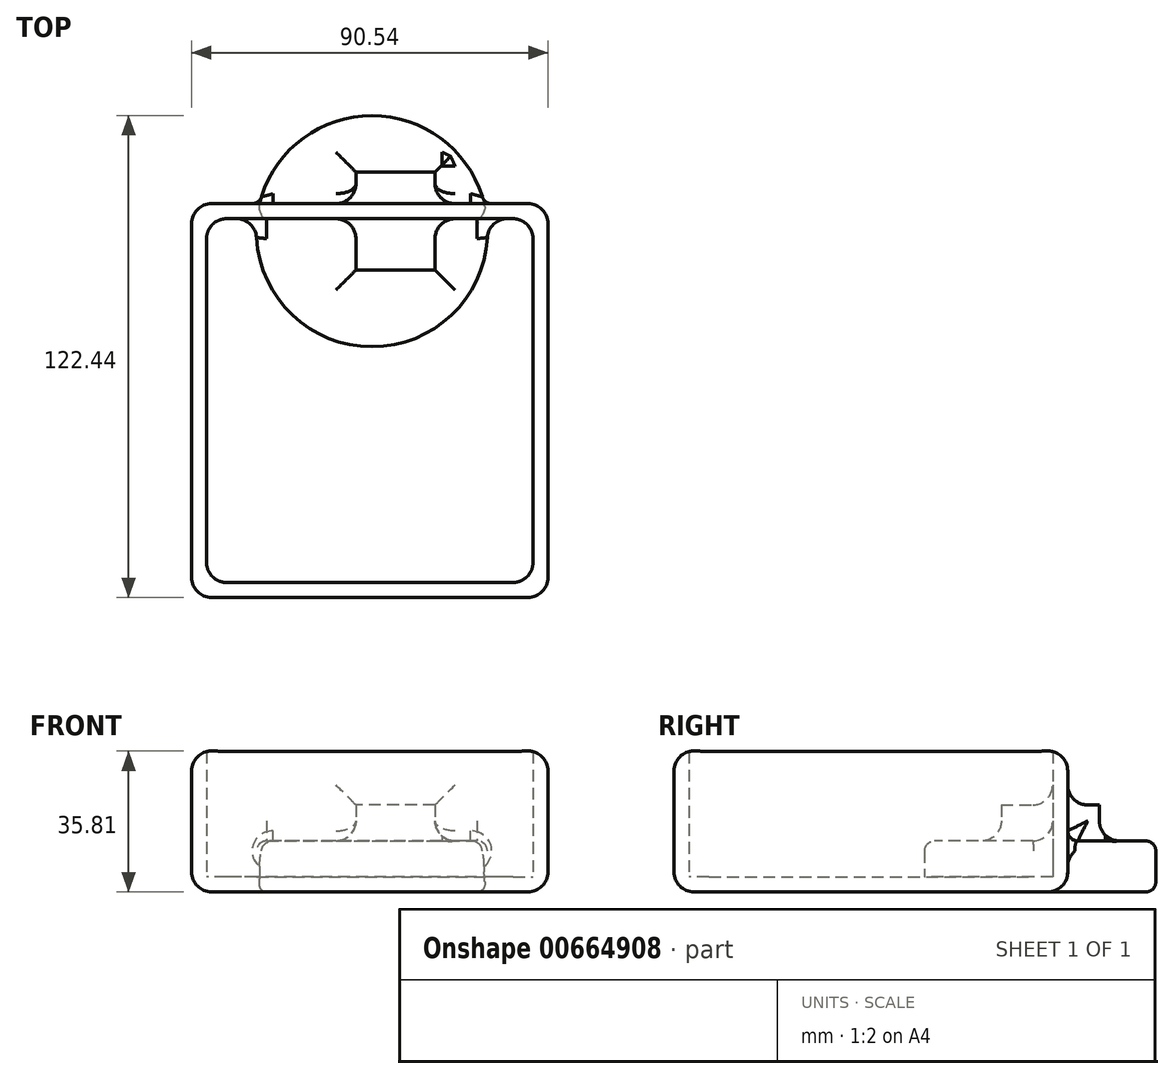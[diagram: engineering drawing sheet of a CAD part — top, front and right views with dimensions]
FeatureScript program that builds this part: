
annotation { "Feature Type Name" : "Feature", "Feature Type Description" : "" }
export const myFeature = defineFeature(function(context is Context, id is Id, definition is map)
    precondition{}
    {
        {
            var Q0;
            Q0=qCreatedBy(makeId("Top.planeOp"),FACE);
            var sketch = newSketch(context, id + "F0", { "sketchPlane" : qUnion([Q0])});
            skLineSegment(sketch, "E0.bottom", {"start": v(36.09, -51.72) * mm, "end": v(-54.45, -51.72) * mm});
            skLineSegment(sketch, "E0.top", {"start": v(36.09, 48.33) * mm, "end": v(-54.45, 48.33) * mm});
            skLineSegment(sketch, "E0.left", {"start": v(36.09, -51.72) * mm, "end": v(36.09, 48.33) * mm});
            skLineSegment(sketch, "E0.right", {"start": v(-54.45, -51.72) * mm, "end": v(-54.45, 48.33) * mm});
            skSolve(sketch);
        }
        {
            var Q0;
            Q0 = qSketchRegion(id + "F0", true);
            extrude(context, id + "F1", {"entities" : qUnion([Q0]), "depth" : 35.81 * mm, "offsetDistance" : 25.4 * mm});
        }
        {
            var Q0;
            Q0=makeQuery(id+"F1.opExtrude","CAP_FACE",FACE,{"disambiguationData":[OSD([sQuery(id+"F0.wireOp",EDGE,"E0.bottom"),sQuery(id+"F0.wireOp",EDGE,"E0.top"),sQuery(id+"F0.wireOp",EDGE,"E0.left"),sQuery(id+"F0.wireOp",EDGE,"E0.right")])],"isStart":false});
            shell(context, id + "F2", {"entities" : qUnion([Q0]), "thickness" : 3.8 * mm});
        }
        {
            var Q0;
            Q0=makeQuery(id+"F1.opExtrude","SWEPT_EDGE",EDGE,{"disambiguationData":[OSD([sQuery(id+"F0.wireOp",EDGE,"E0.bottom"),sQuery(id+"F0.wireOp",EDGE,"E0.left")])]});
            var Q1;
            Q1=makeQuery(id+"F1.opExtrude","SWEPT_EDGE",EDGE,{"disambiguationData":[OSD([sQuery(id+"F0.wireOp",EDGE,"E0.bottom"),sQuery(id+"F0.wireOp",EDGE,"E0.right")])]});
            var Q2;
            Q2=makeQuery(id+"F1.opExtrude","SWEPT_EDGE",EDGE,{"disambiguationData":[OSD([sQuery(id+"F0.wireOp",EDGE,"E0.top"),sQuery(id+"F0.wireOp",EDGE,"E0.left")])]});
            var Q3;
            Q3=makeQuery(id+"F1.opExtrude","SWEPT_EDGE",EDGE,{"disambiguationData":[OSD([sQuery(id+"F0.wireOp",EDGE,"E0.top"),sQuery(id+"F0.wireOp",EDGE,"E0.right")])]});
            var Q4;
            Q4=makeQuery(id+"F2.opShell","OFFSET_EDGE",EDGE,{"disambiguationData":[OSD([sQuery(id+"F0.wireOp",EDGE,"E0.top"),sQuery(id+"F0.wireOp",EDGE,"E0.right")])]});
            var Q5;
            Q5=makeQuery(id+"F2.opShell","OFFSET_EDGE",EDGE,{"disambiguationData":[OSD([sQuery(id+"F0.wireOp",EDGE,"E0.top"),sQuery(id+"F0.wireOp",EDGE,"E0.left")])]});
            var Q6;
            Q6=makeQuery(id+"F2.opShell","OFFSET_EDGE",EDGE,{"disambiguationData":[OSD([sQuery(id+"F0.wireOp",EDGE,"E0.bottom"),sQuery(id+"F0.wireOp",EDGE,"E0.left")])]});
            var Q7;
            Q7=makeQuery(id+"F2.opShell","OFFSET_EDGE",EDGE,{"disambiguationData":[OSD([sQuery(id+"F0.wireOp",EDGE,"E0.bottom"),sQuery(id+"F0.wireOp",EDGE,"E0.right")])]});
            fillet(context, id + "F3", {"entities" : qUnion([Q0, Q1, Q2, Q3, Q4, Q5, Q6, Q7]), "radius" : 5.08 * mm, "tangentPropagation" : true, "allowEdgeOverflow" : false});
        }
        {
            var Q0;
            Q0=makeQuery(id+"F1.opExtrude","CAP_EDGE",EDGE,{"disambiguationData":[OSD([sQuery(id+"F0.wireOp",EDGE,"E0.top")])],"isStart":false});
            var Q1;
            Q1=makeQuery(id+"F1.opExtrude","CAP_EDGE",EDGE,{"disambiguationData":[OSD([sQuery(id+"F0.wireOp",EDGE,"E0.top")])],"isStart":true});
            fillet(context, id + "F4", {"entities" : qUnion([Q0, Q1]), "radius" : 5.08 * mm, "tangentPropagation" : true, "allowEdgeOverflow" : false});
        }
        {
            var Q0;
            Q0=qCreatedBy(makeId("Top.planeOp"),FACE);
            var sketch = newSketch(context, id + "F5", { "sketchPlane" : qUnion([Q0])});
            skCircle(sketch, "E1", {"center": v(-8.63, 41.35) * mm, "radius": 29.37 * mm});
            skSolve(sketch);
        }
        {
            var Q0;
            Q0 = qSketchRegion(id + "F5", true);
            extrude(context, id + "F6", {"entities" : qUnion([Q0]), "operationType" : NewBodyOperationType.ADD, "depth" : 12.95 * mm, "offsetDistance" : 25.4 * mm});
        }
        {
            var Q0;
            {var subQ0=sQuery(id+"F5.wireOp",EDGE,"E1");Q0=makeQuery(id+"F6.boolean.opBoolean","SPLIT",EDGE,{"disambiguationData":[TD([makeQuery(id+"F1.opExtrude","SWEPT_FACE",FACE,{"disambiguationData":[OSD([sQuery(id+"F0.wireOp",EDGE,"E0.top")])]})])],"derivedFrom":makeQuery(id+"F6.opExtrude","CAP_EDGE",EDGE,{"disambiguationData":[OSD([subQ0])],"isStart":false})});}
            var Q1;
            Q1=makeQuery(id+"F6.boolean.opBoolean","INTERSECT",EDGE,{"derivedFrom":[makeQuery(id+"F1.opExtrude","SWEPT_FACE",FACE,{"disambiguationData":[OSD([sQuery(id+"F0.wireOp",EDGE,"E0.top")])]}),makeQuery(id+"F6.opExtrude","CAP_FACE",FACE,{"disambiguationData":[OSD([sQuery(id+"F5.wireOp",EDGE,"E1")])],"isStart":false})]});
            var Q2;
            Q2=makeQuery(id+"F6.opExtrude","CAP_EDGE",EDGE,{"disambiguationData":[OSD([sQuery(id+"F5.wireOp",EDGE,"E1")])],"isStart":true});
            var Q3;
            {var subQ0=sQuery(id+"F5.wireOp",EDGE,"E1");Q3=makeQuery(id+"F6.boolean.opBoolean","SPLIT",EDGE,{"disambiguationData":[TD([makeQuery(id+"F2.opShell","OFFSET_FACE",FACE,{"disambiguationData":[OSD([sQuery(id+"F0.wireOp",EDGE,"E0.top")])]})])],"derivedFrom":makeQuery(id+"F6.opExtrude","CAP_EDGE",EDGE,{"disambiguationData":[OSD([subQ0])],"isStart":false})});}
            fillet(context, id + "F7", {"entities" : qUnion([Q0, Q1, Q2, Q3]), "radius" : 2.54 * mm, "tangentPropagation" : true, "allowEdgeOverflow" : false});
        }
        {
            var Q0;
            Q0=makeQuery(id+"F6.boolean.opBoolean","INTERSECT",EDGE,{"derivedFrom":[makeQuery(id+"F2.opShell","OFFSET_FACE",FACE,{"disambiguationData":[OSD([sQuery(id+"F0.wireOp",EDGE,"E0.top")])]}),makeQuery(id+"F6.opExtrude","CAP_FACE",FACE,{"disambiguationData":[OSD([sQuery(id+"F5.wireOp",EDGE,"E1")])],"isStart":false})]});
            fillet(context, id + "F8", {"entities" : qUnion([Q0]), "radius" : 5.08 * mm, "tangentPropagation" : true, "allowEdgeOverflow" : false});
        }
        {
            var Q0;
            Q0=qCreatedBy(makeId("Top.planeOp"),FACE);
            var sketch = newSketch(context, id + "F9", { "sketchPlane" : qUnion([Q0])});
            skLineSegment(sketch, "E2.bottom", {"start": v(7.4, 31.47) * mm, "end": v(-12.7, 31.47) * mm});
            skLineSegment(sketch, "E2.top", {"start": v(7.4, 56.37) * mm, "end": v(-12.7, 56.37) * mm});
            skLineSegment(sketch, "E2.left", {"start": v(7.4, 31.47) * mm, "end": v(7.4, 56.37) * mm});
            skLineSegment(sketch, "E2.right", {"start": v(-12.7, 31.47) * mm, "end": v(-12.7, 56.37) * mm});
            skSolve(sketch);
        }
        {
            var Q0;
            Q0 = qSketchRegion(id + "F9", true);
            extrude(context, id + "F10", {"entities" : qUnion([Q0]), "operationType" : NewBodyOperationType.ADD, "depth" : 22.1 * mm, "offsetDistance" : 25.4 * mm});
        }
        {
            var Q0;
            Q0=makeQuery(id+"F10.boolean.opBoolean","INTERSECT",EDGE,{"derivedFrom":[makeQuery(id+"F1.opExtrude","SWEPT_FACE",FACE,{"disambiguationData":[OSD([sQuery(id+"F0.wireOp",EDGE,"E0.top")])]}),makeQuery(id+"F10.opExtrude","SWEPT_FACE",FACE,{"disambiguationData":[OSD([sQuery(id+"F9.wireOp",EDGE,"E2.left")])]})]});
            var Q1;
            Q1=makeQuery(id+"F10.boolean.opBoolean","INTERSECT",EDGE,{"derivedFrom":[makeQuery(id+"F1.opExtrude","SWEPT_FACE",FACE,{"disambiguationData":[OSD([sQuery(id+"F0.wireOp",EDGE,"E0.top")])]}),makeQuery(id+"F10.opExtrude","SWEPT_FACE",FACE,{"disambiguationData":[OSD([sQuery(id+"F9.wireOp",EDGE,"E2.right")])]})]});
            var Q2;
            {var subQ0=sQuery(id+"F5.wireOp",EDGE,"E1");Q2=makeQuery(id+"F10.boolean.opBoolean","INTERSECT",EDGE,{"derivedFrom":[makeQuery(id+"F6.boolean.opBoolean","SPLIT",FACE,{"disambiguationData":[TD([makeQuery(id+"F1.opExtrude","SWEPT_FACE",FACE,{"disambiguationData":[OSD([sQuery(id+"F0.wireOp",EDGE,"E0.top")])]})])],"derivedFrom":makeQuery(id+"F6.opExtrude","CAP_FACE",FACE,{"disambiguationData":[OSD([subQ0])],"isStart":false})}),makeQuery(id+"F10.opExtrude","SWEPT_FACE",FACE,{"disambiguationData":[OSD([sQuery(id+"F9.wireOp",EDGE,"E2.top")])]})]});}
            var Q3;
            {var subQ0=sQuery(id+"F5.wireOp",EDGE,"E1");var subQ1=sQuery(id+"F0.wireOp",EDGE,"E0.top");Q3=makeQuery(id+"F10.boolean.opBoolean","INTERSECT",EDGE,{"derivedFrom":[makeQuery(id+"F8.opFillet","BLEND_FACE",FACE,{"disambiguationData":[OSD([subQ1,subQ0]),TDD([makeQuery(id+"F6.boolean.opBoolean","INTERSECT",EDGE,{"derivedFrom":[makeQuery(id+"F2.opShell","OFFSET_FACE",FACE,{"disambiguationData":[OSD([subQ1])]}),makeQuery(id+"F6.opExtrude","CAP_FACE",FACE,{"disambiguationData":[OSD([subQ0])],"isStart":false})]})])]}),makeQuery(id+"F10.opExtrude","SWEPT_FACE",FACE,{"disambiguationData":[OSD([sQuery(id+"F9.wireOp",EDGE,"E2.left")])]})]});}
            var Q4;
            {var subQ0=sQuery(id+"F5.wireOp",EDGE,"E1");var subQ1=sQuery(id+"F0.wireOp",EDGE,"E0.top");Q4=makeQuery(id+"F10.boolean.opBoolean","INTERSECT",EDGE,{"derivedFrom":[makeQuery(id+"F8.opFillet","BLEND_FACE",FACE,{"disambiguationData":[OSD([subQ1,subQ0]),TDD([makeQuery(id+"F6.boolean.opBoolean","INTERSECT",EDGE,{"derivedFrom":[makeQuery(id+"F2.opShell","OFFSET_FACE",FACE,{"disambiguationData":[OSD([subQ1])]}),makeQuery(id+"F6.opExtrude","CAP_FACE",FACE,{"disambiguationData":[OSD([subQ0])],"isStart":false})]})])]}),makeQuery(id+"F10.opExtrude","SWEPT_FACE",FACE,{"disambiguationData":[OSD([sQuery(id+"F9.wireOp",EDGE,"E2.right")])]})]});}
            var Q5;
            {var subQ0=sQuery(id+"F5.wireOp",EDGE,"E1");Q5=makeQuery(id+"F10.boolean.opBoolean","INTERSECT",EDGE,{"derivedFrom":[makeQuery(id+"F6.boolean.opBoolean","SPLIT",FACE,{"disambiguationData":[TD([makeQuery(id+"F2.opShell","OFFSET_FACE",FACE,{"disambiguationData":[OSD([sQuery(id+"F0.wireOp",EDGE,"E0.top")])]})])],"derivedFrom":makeQuery(id+"F6.opExtrude","CAP_FACE",FACE,{"disambiguationData":[OSD([subQ0])],"isStart":false})}),makeQuery(id+"F10.opExtrude","SWEPT_FACE",FACE,{"disambiguationData":[OSD([sQuery(id+"F9.wireOp",EDGE,"E2.bottom")])]})]});}
            var Q6;
            Q6=makeQuery(id+"F10.boolean.opBoolean","INTERSECT",EDGE,{"derivedFrom":[makeQuery(id+"F2.opShell","OFFSET_FACE",FACE,{"disambiguationData":[OSD([sQuery(id+"F0.wireOp",EDGE,"E0.top")])]}),makeQuery(id+"F10.opExtrude","CAP_FACE",FACE,{"disambiguationData":[OSD([sQuery(id+"F9.wireOp",EDGE,"E2.bottom"),sQuery(id+"F9.wireOp",EDGE,"E2.top"),sQuery(id+"F9.wireOp",EDGE,"E2.left"),sQuery(id+"F9.wireOp",EDGE,"E2.right")])],"isStart":false})]});
            var Q7;
            Q7=makeQuery(id+"F10.boolean.opBoolean","INTERSECT",EDGE,{"derivedFrom":[makeQuery(id+"F1.opExtrude","SWEPT_FACE",FACE,{"disambiguationData":[OSD([sQuery(id+"F0.wireOp",EDGE,"E0.top")])]}),makeQuery(id+"F10.opExtrude","CAP_FACE",FACE,{"disambiguationData":[OSD([sQuery(id+"F9.wireOp",EDGE,"E2.bottom"),sQuery(id+"F9.wireOp",EDGE,"E2.top"),sQuery(id+"F9.wireOp",EDGE,"E2.left"),sQuery(id+"F9.wireOp",EDGE,"E2.right")])],"isStart":false})]});
            fillet(context, id + "F11", {"entities" : qUnion([Q0, Q1, Q2, Q3, Q4, Q5, Q6, Q7]), "radius" : 5.08 * mm, "tangentPropagation" : true, "allowEdgeOverflow" : false});
        }
    });
